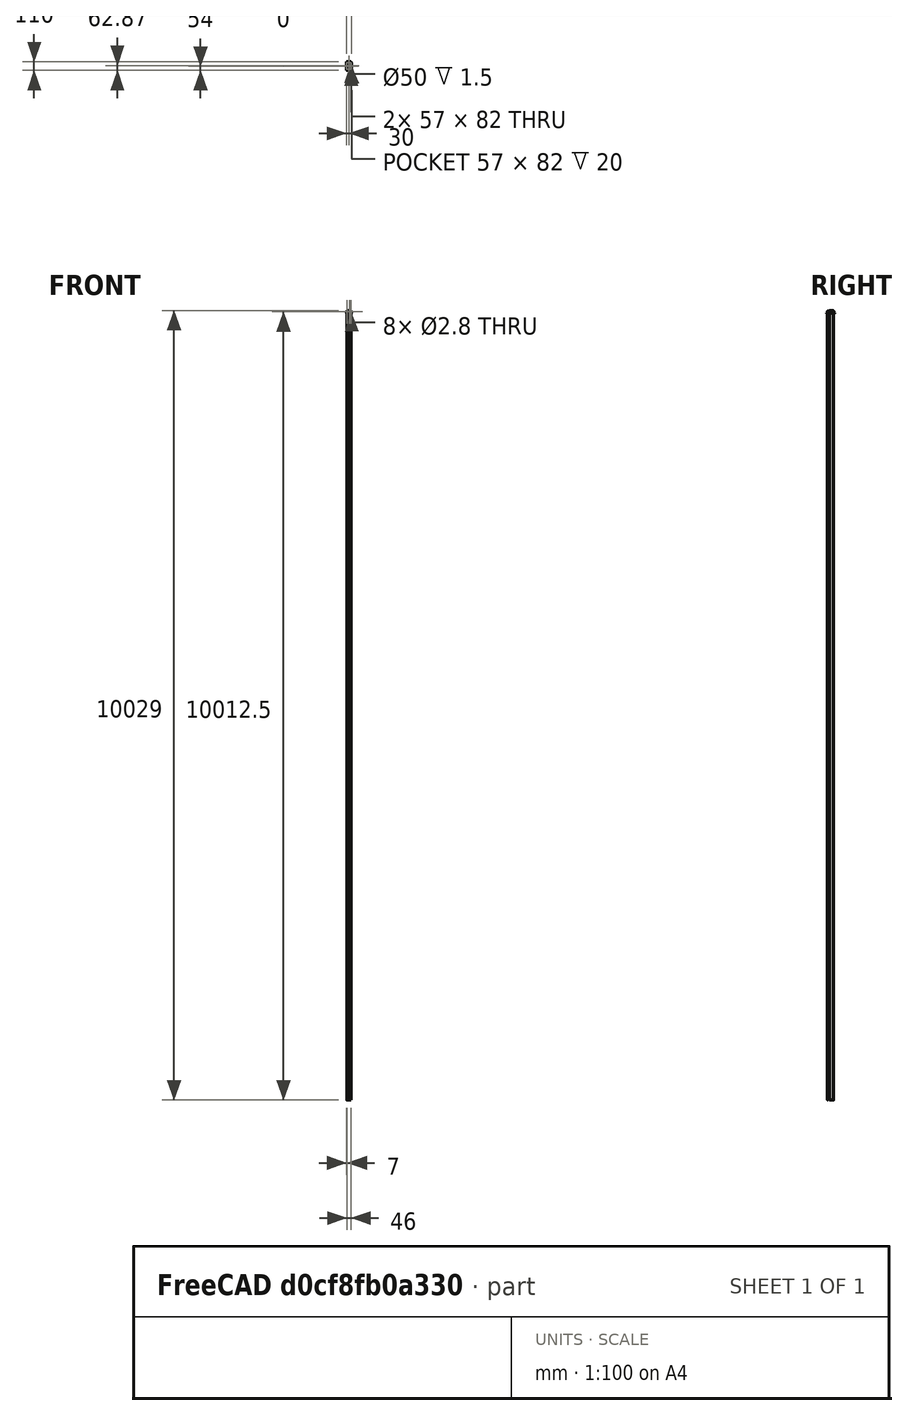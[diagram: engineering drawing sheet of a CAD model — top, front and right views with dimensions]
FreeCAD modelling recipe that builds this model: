
FCSTD DOCUMENT  (FreeCAD 0.16R4733 (Git))
Label: NotifierEnclosure
License: CC-BY 3.0
LicenseURL: http://creativecommons.org/licenses/by/3.0/
objects: Sketcher::SketchObject×9, Part::Box×6, Part::FeaturePython×6, PartDesign::Pad×5, PartDesign::Pocket×4, Part::Cut×4, Part::MultiFuse×3, App::DocumentObjectGroup×2, Part::Thickness×2, Part::Part2DObjectPython×2, PartDesign::Fillet×2, Part::Offset×2, Part::Cylinder×1, Part::Fillet×1
note: 56 computed .brp shape members not serialized (recipe doc carries the construction recipe); baked Part::Feature solids carry a one-line shape summary decoded from their .brp

FEATURE [Part::Box] Box  label="Cube"
  Height = 20
  Length = 57
  Width = 82
FEATURE [Part::Box] Box001  label="Base"
  Height = 1.6
  Length = 54
  Placement = pos=(0,0,3) rot=(0,0,1;0rad)
  Width = 80
FEATURE [Part::Box] Box002  label="EthernetJack"
  Height = 13.6
  Length = 16
  Placement = pos=(11.2,-4.6,4.6) rot=(0,0,1;0rad)
  Width = 21
FEATURE [Part::Box] Box003  label="PowerJack"
  Height = 11
  Length = 9
  Placement = pos=(43.4,-4.5,4.6) rot=(0,0,1;0rad)
  Width = 14.5
FEATURE [Sketcher::SketchObject] Sketch
  ExternalGeometry = -> [Box001]
  Placement = pos=(0,0,4.6) rot=(0,0,1;0rad)
  Support = -> Box001 [Face6]
  sketch-geometry (6):
    g0: Circle CenterX=2.2 CenterY=77.12 CenterZ=0 NormalX=0 NormalY=0 NormalZ=1 Radius=1.5
    g1: Circle CenterX=50.25 CenterY=76.75 CenterZ=0 NormalX=0 NormalY=0 NormalZ=1 Radius=1.5
    g2: Circle CenterX=2 CenterY=2.7 CenterZ=0 NormalX=0 NormalY=0 NormalZ=1 Radius=1.5
    g3: Circle CenterX=39.8 CenterY=2.7 CenterZ=0 NormalX=0 NormalY=0 NormalZ=1 Radius=1.5
    g4: LineSegment [constr] StartX=0.5 StartY=1.2 StartZ=0 EndX=0.5 EndY=5.19188 EndZ=0
    g5: LineSegment [constr] StartX=0.5 StartY=1.2 StartZ=0 EndX=4.53205 EndY=1.2 EndZ=0
  constraints (17):
    c: Radius(g2) = 1.5
    c: Vertical(g4)
    c: Tangent(g4,g2)
    c: Horizontal(g5)
    c: Tangent(g5,g2)
    c: Coincident(g4,g5)
    c: DistanceX(g-1,g4) = 0.5
    c: DistanceY(g-1,g5) = 1.2
    c: Equal(g3,g2)
    c: DistanceY(g-1,g3) = 2.7
    c: DistanceX(g3,g-3) = 14.2
    c: Equal(g0,g1)
    c: Equal(g1,g2)
    c: DistanceY(g0,g-4) = 2.88
    c: DistanceX(g0,g-4) = -2.2
    c: DistanceX(g1,g-4) = 3.75
    c: DistanceY(g1,g-4) = 3.25
FEATURE [PartDesign::Pocket] Pocket  label="Holes"
  Length = 5
  Placement = pos=(0,0,3) rot=(0,0,1;0rad)
  Sketch = -> Sketch
  Type = 1
FEATURE [App::DocumentObjectGroup] Group  label="iBoard"
  Group = -> [Box001,Box002,Box003,Pocket]
FEATURE [Part::Thickness] Thickness
  Faces = -> Box [Face6]
  Intersection = false
  Join = 0
  Mode = 0
  Placement = pos=(-1.5,0,0) rot=(0,0,1;0rad)
  SelfIntersection = false
  Value = 1.5
FEATURE [Sketcher::SketchObject] Sketch001
  ExternalGeometry = -> [Thickness]
  Placement = pos=(-1.5,0,20) rot=(0,0,1;0rad)
  Support = -> Thickness [Face6]
  sketch-geometry (8):
    g0: LineSegment StartX=-1.5 StartY=0 StartZ=0 EndX=-1.5 EndY=82 EndZ=0
    g1: LineSegment StartX=0 StartY=83.5 StartZ=0 EndX=57 EndY=83.5 EndZ=0
    g2: LineSegment StartX=58.5 StartY=0 StartZ=0 EndX=58.5 EndY=82 EndZ=0
    g3: LineSegment StartX=0 StartY=-1.5 StartZ=0 EndX=57 EndY=-1.5 EndZ=0
    g4: ArcOfCircle CenterX=0 CenterY=0 CenterZ=0 NormalX=0 NormalY=0 NormalZ=1 Radius=1.5 StartAngle=3.14159 EndAngle=4.71239
    g5: ArcOfCircle CenterX=0 CenterY=82 CenterZ=0 NormalX=0 NormalY=0 NormalZ=1 Radius=1.5 StartAngle=1.5708 EndAngle=3.14159
    g6: ArcOfCircle CenterX=57 CenterY=82 CenterZ=0 NormalX=0 NormalY=0 NormalZ=1 Radius=1.5 StartAngle=0 EndAngle=1.5708
    g7: ArcOfCircle CenterX=57 CenterY=0 CenterZ=0 NormalX=0 NormalY=0 NormalZ=1 Radius=1.5 StartAngle=4.71239 EndAngle=6.28319
  constraints (24):
    c: Vertical(g0)
    c: Horizontal(g1)
    c: Vertical(g2)
    c: Horizontal(g3)
    c: Coincident(g0,g-10)
    c: Coincident(g0,g-4)
    c: Coincident(g-10,g3)
    c: Coincident(g3,g-9)
    c: Coincident(g2,g-8)
    c: Coincident(g2,g-7)
    c: Coincident(g1,g-6)
    c: Coincident(g1,g-5)
    c: Coincident(g4,g-1)
    c: Coincident(g4,g3)
    c: Coincident(g4,g0)
    c: Coincident(g5,g-3)
    c: Coincident(g5,g0)
    c: Coincident(g5,g1)
    c: Coincident(g6,g-6)
    c: Coincident(g6,g1)
    c: Coincident(g6,g2)
    c: Coincident(g7,g-8)
    c: Coincident(g7,g2)
    c: Coincident(g7,g3)
FEATURE [Part::Part2DObjectPython] Clone2D  label="Clone of Sketch001 (2D)"  # Draft 2D object (typed FeaturePython)
  Objects = -> [Sketch001]
  Placement = pos=(-1.5,0,20) rot=(0,0,1;0rad)
  Scale = (1,1,1)
FEATURE [PartDesign::Pad] Pad
  Length = 1.5
  Length2 = 100
  Placement = pos=(-1.5,0,20) rot=(0,0,1;0rad)
  Sketch = -> Clone2D
  Type = 0
FEATURE [PartDesign::Fillet] Fillet
  Base = -> Pad [Edge22,Edge24,Edge19,Edge13,Edge7,Edge4,Edge16,Edge10]
  Placement = pos=(-1.5,0,20) rot=(0,0,1;0rad)
  Radius = 0.5
FEATURE [Sketcher::SketchObject] Sketch002
  ExternalGeometry = -> [Fillet]
  Placement = pos=(-1.5,0,21.5) rot=(0,0,1;0rad)
  Support = -> Fillet [Face8]
  sketch-geometry (2):
    g0: Circle CenterX=28.5 CenterY=49.8696 CenterZ=0 NormalX=0 NormalY=0 NormalZ=1 Radius=25
    g1: LineSegment [constr] StartX=28.5 StartY=49.8696 StartZ=0 EndX=28.5 EndY=88.1673 EndZ=0
  constraints (4):
    c: Radius(g0) = 25
    c: Coincident(g1,g0)
    c: Vertical(g1)
    c: Symmetric(g-5,g-3,g1)
FEATURE [PartDesign::Pocket] Pocket001
  Length = 5
  Placement = pos=(-1.5,0,20) rot=(0,0,1;0rad)
  Sketch = -> Sketch002
  Type = 1
FEATURE [Sketcher::SketchObject] Sketch003
  Placement = pos=(-1.5,0,0) rot=(0,0,1;0rad)
  Support = -> Thickness [Face5]
  sketch-geometry (4):
    g0: Circle CenterX=3.53528 CenterY=2.63614 CenterZ=0 NormalX=0 NormalY=0 NormalZ=1 Radius=2.5
    g1: Circle CenterX=41.3722 CenterY=2.74074 CenterZ=0 NormalX=0 NormalY=0 NormalZ=1 Radius=2.5
    g2: Circle CenterX=3.78181 CenterY=77.146 CenterZ=0 NormalX=0 NormalY=0 NormalZ=1 Radius=2.5
    g3: Circle CenterX=51.8469 CenterY=76.7239 CenterZ=0 NormalX=0 NormalY=0 NormalZ=1 Radius=2.5
  constraints (4):
    c: Radius(g0) = 2.5
    c: Equal(g0,g1)
    c: Equal(g1,g2)
    c: Equal(g2,g3)
FEATURE [PartDesign::Pad] Pad001
  Length = 3
  Length2 = 100
  Placement = pos=(-1.5,0,0) rot=(0,0,1;0rad)
  Sketch = -> Sketch003
  Type = 0
FEATURE [Sketcher::SketchObject] Sketch004
  ExternalGeometry = -> [Pad001]
  Placement = pos=(-1.5,0,3) rot=(0,0,1;0rad)
  Support = -> Pad001 [Face30]
  sketch-geometry (4):
    g0: Circle CenterX=3.78181 CenterY=77.146 CenterZ=0 NormalX=0 NormalY=0 NormalZ=1 Radius=1.4
    g1: Circle CenterX=51.8469 CenterY=76.7239 CenterZ=0 NormalX=0 NormalY=0 NormalZ=1 Radius=1.4
    g2: Circle CenterX=3.53528 CenterY=2.63614 CenterZ=0 NormalX=0 NormalY=0 NormalZ=1 Radius=1.4
    g3: Circle CenterX=41.3722 CenterY=2.74074 CenterZ=0 NormalX=0 NormalY=0 NormalZ=1 Radius=1.4
  constraints (8):
    c: Coincident(g0,g-3)
    c: Coincident(g1,g-4)
    c: Coincident(g2,g-5)
    c: Coincident(g3,g-6)
    c: Radius(g1) = 1.4
    c: Equal(g1,g0)
    c: Equal(g0,g2)
    c: Equal(g2,g3)
FEATURE [PartDesign::Pocket] Pocket002
  Length = 3
  Placement = pos=(-1.5,0,0) rot=(0,0,1;0rad)
  Sketch = -> Sketch004
  Type = 0
FEATURE [Sketcher::SketchObject] Sketch005
  ExternalGeometry = -> [Pocket001]
  Placement = pos=(-1.5,0,20) rot=(1,0,0;3.14159rad)
  Support = -> Pocket001 [Face4]
  sketch-geometry (8):
    g0: LineSegment StartX=0 StartY=0 StartZ=0 EndX=57 EndY=0 EndZ=0
    g1: LineSegment StartX=57 StartY=0 StartZ=0 EndX=57 EndY=-82 EndZ=0
    g2: LineSegment StartX=57 StartY=-82 StartZ=0 EndX=0 EndY=-82 EndZ=0
    g3: LineSegment StartX=0 StartY=-82 StartZ=0 EndX=0 EndY=0 EndZ=0
    g4: LineSegment StartX=1.5 StartY=-1.5 StartZ=0 EndX=55.5 EndY=-1.5 EndZ=0
    g5: LineSegment StartX=55.5 StartY=-1.5 StartZ=0 EndX=55.5 EndY=-80.5 EndZ=0
    g6: LineSegment StartX=55.5 StartY=-80.5 StartZ=0 EndX=1.5 EndY=-80.5 EndZ=0
    g7: LineSegment StartX=1.5 StartY=-80.5 StartZ=0 EndX=1.5 EndY=-1.5 EndZ=0
  constraints (22):
    c: Coincident(g0,g1)
    c: Coincident(g1,g2)
    c: Coincident(g2,g3)
    c: Coincident(g3,g0)
    c: Horizontal(g0)
    c: Horizontal(g2)
    c: Vertical(g1)
    c: Vertical(g3)
    c: Coincident(g0,g-1)
    c: Coincident(g1,g-6)
    c: Coincident(g4,g5)
    c: Coincident(g5,g6)
    c: Coincident(g6,g7)
    c: Coincident(g7,g4)
    c: Horizontal(g4)
    c: Horizontal(g6)
    c: Vertical(g5)
    c: Vertical(g7)
    c: DistanceX(g6,g2) = -1.5
    c: DistanceX(g5,g1) = 1.5
    c: DistanceY(g5,g1) = -1.5
    c: DistanceY(g4,g0) = 1.5
FEATURE [PartDesign::Pad] Pad002
  Length = 2
  Length2 = 100
  Placement = pos=(-1.5,0,20) rot=(0,0,1;0rad)
  Sketch = -> Sketch005
  Type = 0
FEATURE [App::DocumentObjectGroup] Group001  label="Lid"
  Group = -> [Pad,Fillet,Pocket001,Pad002]
FEATURE [Part::Box] Box004  label="Tab1"
  Height = 10
  Length = 8
  Placement = pos=(0,0,8) rot=(0,0,1;0rad)
  Width = 1.5
FEATURE [Part::FeaturePython] Clone  label="Clone of Tab1"  # Draft clone (typed FeaturePython)
  Objects = -> [Box004]
  Placement = pos=(32,0,8) rot=(0,0,1;0rad)
  Scale = (1,1,1)
FEATURE [Part::FeaturePython] Clone001  label="Clone of Tab002"  # Draft clone (typed FeaturePython)
  Objects = -> [Box004]
  Placement = pos=(0,80.5,8) rot=(0,0,1;0rad)
  Scale = (1,1,1)
FEATURE [Part::FeaturePython] Clone002  label="Clone of Tab003"  # Draft clone (typed FeaturePython)
  Objects = -> [Box004]
  Placement = pos=(46,80.5,8) rot=(0,0,1;0rad)
  Scale = (1,1,1)
FEATURE [Part::Cylinder] Cylinder
  Angle = 360
  Height = 10
  Placement = pos=(4,6,14) rot=(1,0,0;1.5708rad)
  Radius = 1.4
FEATURE [Part::MultiFuse] Fusion  label="LidFusion"
  Shapes = -> [Pad002,Box004,Clone,Clone001,Clone002]
FEATURE [Part::FeaturePython] Clone003  label="Clone of Cylinder"  # Draft clone (typed FeaturePython)
  Objects = -> [Cylinder]
  Placement = pos=(36,6,14) rot=(1,0,0;1.5708rad)
  Scale = (1,1,1)
FEATURE [Part::FeaturePython] Clone004  label="Clone of Cylinder001"  # Draft clone (typed FeaturePython)
  Objects = -> [Cylinder]
  Placement = pos=(4,86,14) rot=(1,0,0;1.5708rad)
  Scale = (1,1,1)
FEATURE [Part::FeaturePython] Clone005  label="Clone of Cylinder002"  # Draft clone (typed FeaturePython)
  Objects = -> [Cylinder]
  Placement = pos=(50,86,14) rot=(1,0,0;1.5708rad)
  Scale = (1,1,1)
FEATURE [Part::MultiFuse] Fusion001
  Shapes = -> [Clone005,Clone004,Clone003,Cylinder]
FEATURE [Part::Cut] Cut
  Base = -> Fusion
  Tool = -> Fusion001
FEATURE [Part::Cut] Cut001
  Base = -> Pocket002
  Tool = -> Fusion001
FEATURE [Part::Offset] Offset
  Fill = false
  Intersection = false
  Join = 2
  Mode = 0
  SelfIntersection = false
  Source = -> Box002
  Value = 1
FEATURE [Part::Offset] Offset001
  Fill = false
  Intersection = false
  Join = 2
  Mode = 0
  SelfIntersection = false
  Source = -> Box003
  Value = 1
FEATURE [Part::MultiFuse] Fusion002
  Shapes = -> [Offset,Offset001]
FEATURE [Part::Cut] Cut002
  Base = -> Cut001
  Tool = -> Fusion002
FEATURE [Part::Cut] Cut003
  Base = -> Cut
  Tool = -> Offset
FEATURE [Sketcher::SketchObject] Sketch006
  ExternalGeometry = -> [Cut003]
  Placement = pos=(0,0,21.5) rot=(0,0,1;0rad)
  Support = -> Cut003 [Face60]
  sketch-geometry (1):
    g0: Circle CenterX=27 CenterY=49.8696 CenterZ=0 NormalX=0 NormalY=0 NormalZ=1 Radius=24.5
  constraints (2):
    c: Coincident(g0,g-3)
    c: Radius(g0) = 24.5
FEATURE [Part::Part2DObjectPython] Clone2D001  label="Clone of Sketch006 (2D)"  # Draft 2D object (typed FeaturePython)
  Objects = -> [Sketch006]
  Placement = pos=(0,0,20.5) rot=(0,0,1;0rad)
  Scale = (1,1,1)
FEATURE [PartDesign::Pad] Pad003
  Length = 10
  Length2 = 100
  Placement = pos=(0,0,20.5) rot=(0,0,1;0rad)
  Sketch = -> Clone2D001
  Type = 0
FEATURE [PartDesign::Fillet] Fillet001
  Base = -> Pad003 [Edge3]
  Placement = pos=(0,0,20.5) rot=(0,0,1;0rad)
  Radius = 5
FEATURE [Sketcher::SketchObject] Sketch007
  ExternalGeometry = -> [Fillet001]
  Placement = pos=(0,0,20.5) rot=(1,0,0;3.14159rad)
  Support = -> Fillet001 [Face3]
  sketch-geometry (1):
    g0: Circle CenterX=27 CenterY=-49.8696 CenterZ=0 NormalX=0 NormalY=0 NormalZ=1 Radius=26.5
  constraints (2):
    c: Coincident(g0,g-3)
    c: Radius(g0) = 26.5
FEATURE [PartDesign::Pad] Pad004
  Length = 1.5
  Length2 = 100
  Placement = pos=(0,0,20.5) rot=(0,0,1;0rad)
  Sketch = -> Sketch007
  Type = 0
FEATURE [Part::Thickness] Thickness001
  Faces = -> Pad004 [Face3]
  Intersection = false
  Join = 0
  Mode = 0
  SelfIntersection = false
  Value = -1.5
FEATURE [Part::Box] Box005  label="Cube001"
  Height = 1.5
  Length = 58
  Placement = pos=(-2,-13,-1.5) rot=(0,0,1;0rad)
  Width = 110
FEATURE [Part::Fillet] Fillet002
  Base = -> Box005
  Edges = 4 edges r=5: [Edge1,Edge3,Edge5,Edge7]
FEATURE [Sketcher::SketchObject] Sketch008
  ExternalGeometry = -> [Fillet002]
  Support = -> Fillet002 [Face2]
  sketch-geometry (4):
    g0: Circle CenterX=3 CenterY=92 CenterZ=0 NormalX=0 NormalY=0 NormalZ=1 Radius=1.5
    g1: Circle CenterX=51 CenterY=92 CenterZ=0 NormalX=0 NormalY=0 NormalZ=1 Radius=1.5
    g2: Circle CenterX=3 CenterY=-8 CenterZ=0 NormalX=0 NormalY=0 NormalZ=1 Radius=1.5
    g3: Circle CenterX=51 CenterY=-8 CenterZ=0 NormalX=0 NormalY=0 NormalZ=1 Radius=1.5
  constraints (8):
    c: Radius(g0) = 1.5
    c: Equal(g0,g1)
    c: Equal(g1,g3)
    c: Equal(g3,g2)
    c: Coincident(g2,g-6)
    c: Coincident(g3,g-5)
    c: Coincident(g0,g-3)
    c: Coincident(g1,g-4)
FEATURE [PartDesign::Pocket] Pocket003
  Length = 5
  Sketch = -> Sketch008
  Type = 0
